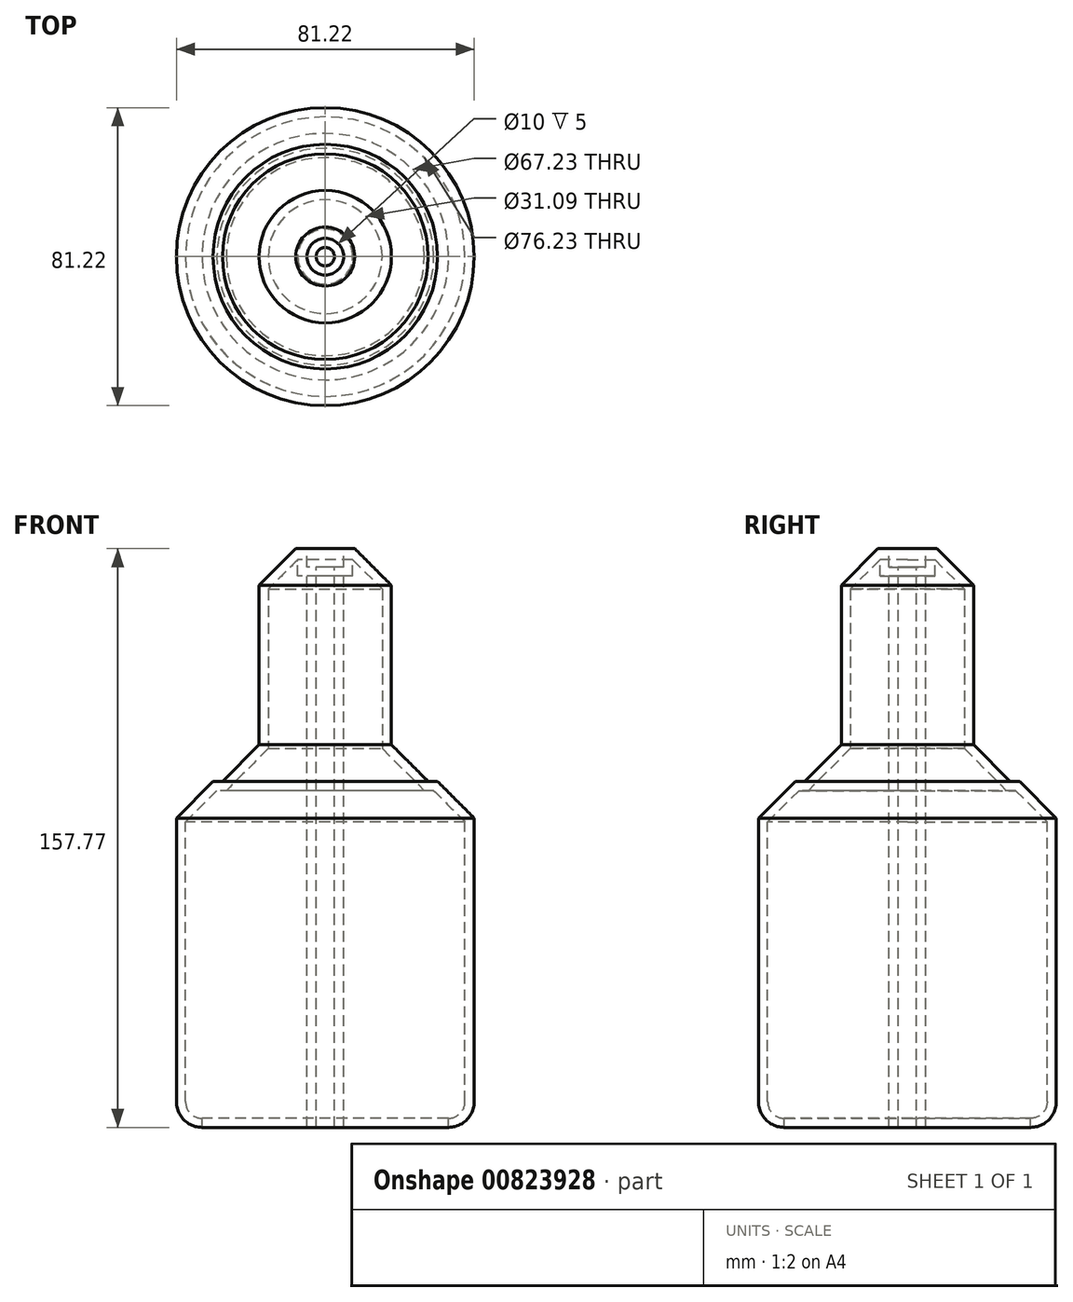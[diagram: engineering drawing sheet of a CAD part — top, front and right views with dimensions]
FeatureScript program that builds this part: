
annotation { "Feature Type Name" : "Feature", "Feature Type Description" : "" }
export const myFeature = defineFeature(function(context is Context, id is Id, definition is map)
    precondition{}
    {
        {
            var Q0;
            Q0=qCreatedBy(makeId("Top.planeOp"),FACE);
            var sketch = newSketch(context, id + "F0", { "sketchPlane" : qUnion([Q0])});
            skCircle(sketch, "E0", {"center": v(0, 0) * mm, "radius": 18.04 * mm});
            skSolve(sketch);
        }
        {
            var Q0;
            Q0=makeQuery(id+"F0.imprint","IMPRINT",FACE,{"disambiguationData":[TD([[makeQuery(id+"F0.imprint","IMPRINT",EDGE,{"derivedFrom":sQuery(id+"F0.wireOp",EDGE,"E0")}),1.0]])]});
            extrude(context, id + "F1", {"entities" : qUnion([Q0]), "endBound" : BoundingType.SYMMETRIC, "depth" : 127 * mm, "offsetDistance" : 25.4 * mm, "hasSecondDirection" : true, "secondDirectionOppositeDirection" : true, "secondDirectionDepth" : 127 * mm});
        }
        {
            var Q0;
            Q0=qCreatedBy(makeId("Front.planeOp"),FACE);
            var sketch = newSketch(context, id + "F2", { "sketchPlane" : qUnion([Q0])});
            skLineSegment(sketch, "E1.bottom", {"start": v(0.32, 0.06) * mm, "end": v(40.61, 0.06) * mm});
            skLineSegment(sketch, "E1.top", {"start": v(0.32, -94.27) * mm, "end": v(40.61, -94.27) * mm});
            skLineSegment(sketch, "E1.left", {"start": v(0.32, 0.06) * mm, "end": v(0.32, -94.27) * mm});
            skLineSegment(sketch, "E1.right", {"start": v(40.61, 0.06) * mm, "end": v(40.61, -94.27) * mm});
            skSolve(sketch);
        }
        {
            var Q0;
            Q0 = qSketchRegion(id + "F2", true);
            var Q1;
            Q1=makeQuery(id+"F1.opExtrude","SWEPT_FACE",FACE,{"disambiguationData":[OSD([sQuery(id+"F0.wireOp",EDGE,"E0")])]});
            revolve(context, id + "F3", {"operationType" : NewBodyOperationType.ADD, "surfaceOperationType" : NewSurfaceOperationType.NEW, "entities" : qUnion([Q0]), "axis" : qUnion([Q1]), "revolveType" : RevolveType.FULL});
        }
        {
            var Q0;
            Q0=makeQuery(id+"F3.opRevolve","SWEPT_EDGE",EDGE,{"disambiguationData":[OSD([sQuery(id+"F2.wireOp",EDGE,"E1.bottom"),sQuery(id+"F2.wireOp",EDGE,"E1.right")])]});
            var Q1;
            Q1=makeQuery(id+"F1.opExtrude","SWEPT_FACE",FACE,{"disambiguationData":[OSD([sQuery(id+"F0.wireOp",EDGE,"E0")])]});
            chamfer(context, id + "F4", {"entities" : qUnion([Q0, Q1]), "width" : 10 * mm, "tangentPropagation" : true});
        }
        {
            var Q0;
            Q0=makeQuery(id+"F1.opExtrude","CAP_FACE",FACE,{"disambiguationData":[OSD([sQuery(id+"F0.wireOp",EDGE,"E0")])],"isStart":false});
            var sketch = newSketch(context, id + "F5", { "sketchPlane" : qUnion([Q0])});
            skPoint(sketch, "E2", {"position": v(0, 0) * mm});
            skPoint(sketch, "E3", {"position": v(-4.17, -49.72) * mm});
            skSolve(sketch);
        }
        {
            var Q0;
            Q0=sQuery(id+"F5.wireOp",VERTEX,"E2");
            var Q1;
            Q1=makeQuery(id+"F1.opExtrude","SWEPT_BODY",BODY,{"disambiguationData":[OSD([sQuery(id+"F0.wireOp",EDGE,"E0")])]});
            hole(context, id + "F6", {"style" : HoleStyle.C_BORE, "endStyle" : HoleEndStyle.THROUGH, "holeDiameter" : 5 * mm, "cBoreDiameter" : 10 * mm, "cBoreDepth" : 5 * mm, "majorDiameter" : 5 * mm, "isTappedThrough" : true, "tappedDepth" : 12 * mm, "tapClearance" : 3, "locations" : qUnion([Q0]), "scope" : qUnion([Q1])});
        }
        {
            var Q0;
            Q0=makeQuery(id+"F3.opRevolve","SWEPT_EDGE",EDGE,{"disambiguationData":[OSD([sQuery(id+"F2.wireOp",EDGE,"E1.top"),sQuery(id+"F2.wireOp",EDGE,"E1.right")])]});
            fillet(context, id + "F7", {"entities" : qUnion([Q0]), "radius" : 7 * mm, "tangentPropagation" : true, "allowEdgeOverflow" : false});
        }
        {
            var Q0;
            Q0=makeQuery(id+"F3.opRevolve","SWEPT_FACE",FACE,{"disambiguationData":[OSD([sQuery(id+"F2.wireOp",EDGE,"E1.top")])]});
            shell(context, id + "F8", {"entities" : qUnion([Q0]), "thickness" : 2.5 * mm});
        }
    });
